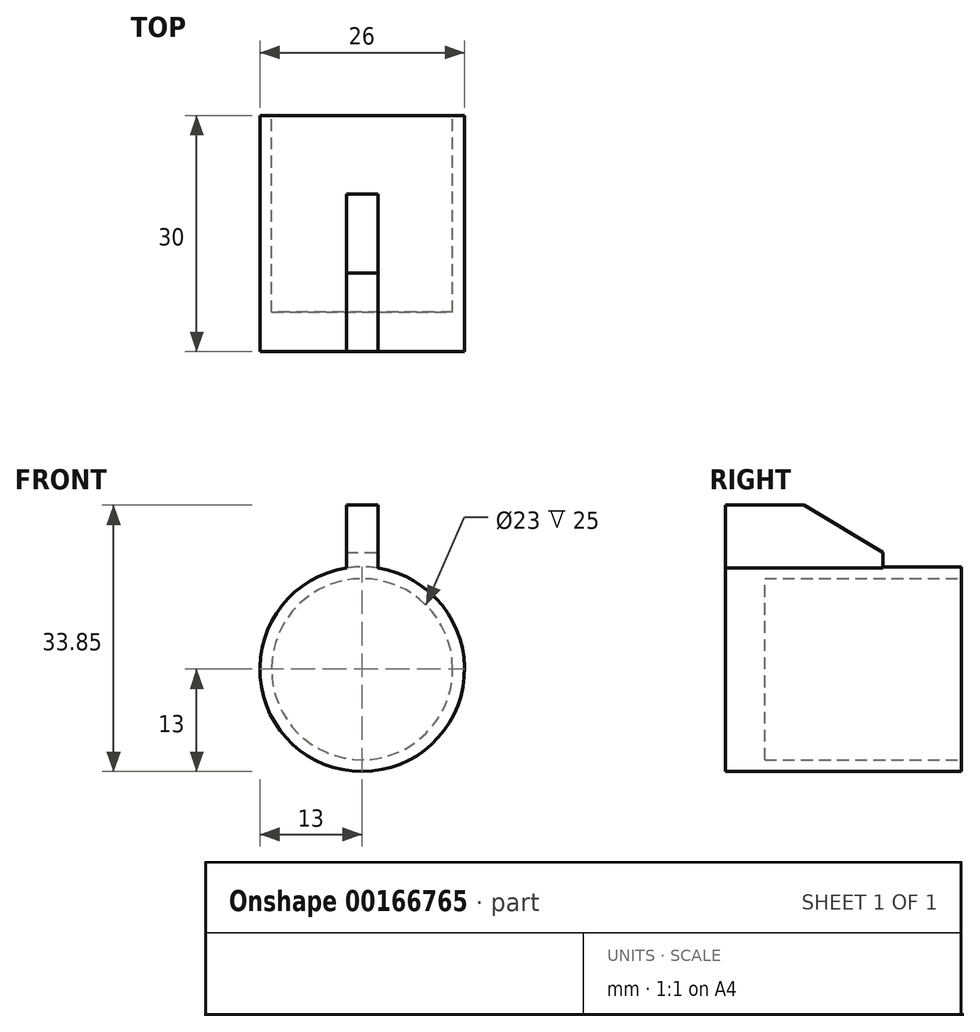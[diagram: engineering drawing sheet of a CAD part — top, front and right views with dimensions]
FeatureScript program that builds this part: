
annotation { "Feature Type Name" : "Feature", "Feature Type Description" : "" }
export const myFeature = defineFeature(function(context is Context, id is Id, definition is map)
    precondition{}
    {
        {
            var Q0;
            Q0=qCreatedBy(makeId("Front.planeOp"),FACE);
            var sketch = newSketch(context, id + "F0", { "sketchPlane" : qUnion([Q0])});
            skCircle(sketch, "E0", {"center": v(0, 0) * mm, "radius": 13 * mm});
            skSolve(sketch);
        }
        {
            var Q0;
            Q0 = qSketchRegion(id + "F0", true);
            extrude(context, id + "F1", {"entities" : qUnion([Q0]), "depth" : 30 * mm});
        }
        {
            var Q0;
            Q0=qCreatedBy(makeId("Front.planeOp"),FACE);
            var sketch = newSketch(context, id + "F2", { "sketchPlane" : qUnion([Q0])});
            skCircle(sketch, "E1", {"center": v(0, 0) * mm, "radius": 11.5 * mm});
            skSolve(sketch);
        }
        {
            var Q0;
            Q0 = qSketchRegion(id + "F2", true);
            extrude(context, id + "F3", {"entities" : qUnion([Q0]), "operationType" : NewBodyOperationType.REMOVE, "depth" : 25 * mm});
        }
        {
            var Q0;
            Q0=makeQuery(id+"F1.opExtrude","CAP_FACE",FACE,{"disambiguationData":[OSD([sQuery(id+"F0.wireOp",EDGE,"E0")])],"isStart":false});
            var sketch = newSketch(context, id + "F4", { "sketchPlane" : qUnion([Q0])});
            skLineSegment(sketch, "E2.bottom", {"start": v(2, 12.85) * mm, "end": v(-2, 12.85) * mm});
            skLineSegment(sketch, "E2.top", {"start": v(2, 20.85) * mm, "end": v(-2, 20.85) * mm});
            skLineSegment(sketch, "E2.left", {"start": v(2, 12.85) * mm, "end": v(2, 20.85) * mm});
            skLineSegment(sketch, "E2.right", {"start": v(-2, 12.85) * mm, "end": v(-2, 20.85) * mm});
            skPoint(sketch, "E2.middle", {"position": v(0, 16.85) * mm});
            skPoint(sketch, "E3", {"position": v(-2, 12.85) * mm});
            skPoint(sketch, "E4", {"position": v(2, 12.85) * mm});
            skSolve(sketch);
        }
        {
            var Q0;
            Q0 = qSketchRegion(id + "F4", true);
            extrude(context, id + "F5", {"entities" : qUnion([Q0]), "operationType" : NewBodyOperationType.ADD, "oppositeDirection" : true, "depth" : 20 * mm});
        }
        {
            var Q0;
            Q0=makeQuery(id+"F5.opExtrude","SWEPT_FACE",FACE,{"disambiguationData":[OSD([sQuery(id+"F4.wireOp",EDGE,"E2.left")])]});
            var sketch = newSketch(context, id + "F6", { "sketchPlane" : qUnion([Q0])});
            skLineSegment(sketch, "E5", {"start": v(-20, 20.85) * mm, "end": v(-10, 14.85) * mm});
            skLineSegment(sketch, "E6", {"start": v(-10, 14.85) * mm, "end": v(-10, 20.85) * mm});
            skLineSegment(sketch, "E7", {"start": v(-10, 20.85) * mm, "end": v(-20, 20.85) * mm});
            skSolve(sketch);
        }
        {
            var Q0;
            Q0 = qSketchRegion(id + "F6", true);
            extrude(context, id + "F7", {"entities" : qUnion([Q0]), "operationType" : NewBodyOperationType.REMOVE, "oppositeDirection" : true, "depth" : 4 * mm});
        }
    });
